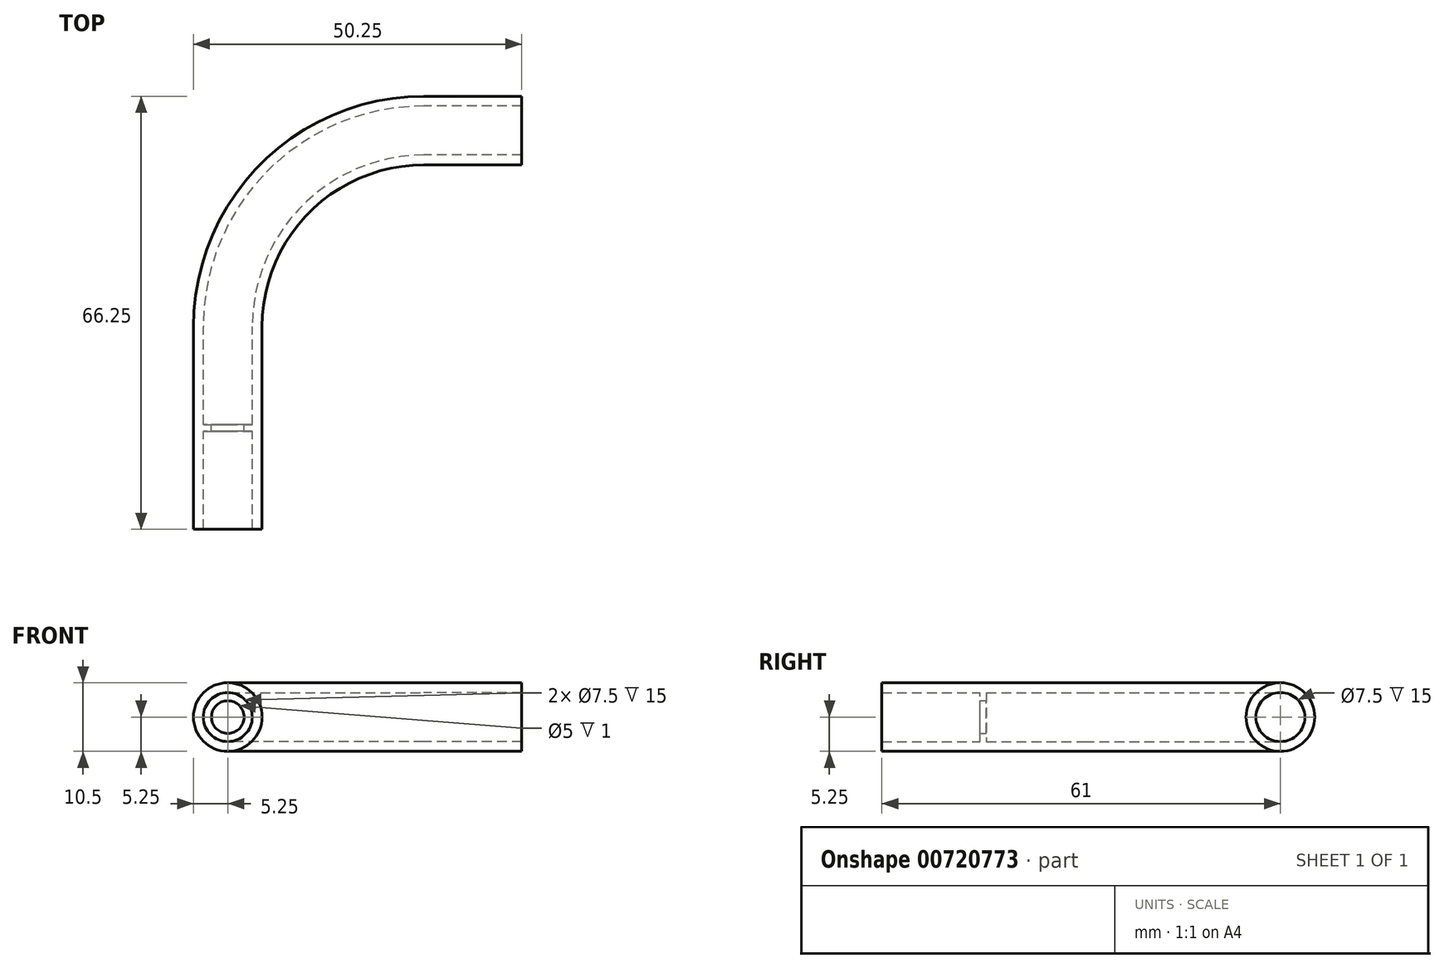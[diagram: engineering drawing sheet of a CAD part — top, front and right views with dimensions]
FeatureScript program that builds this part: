
annotation { "Feature Type Name" : "Feature", "Feature Type Description" : "" }
export const myFeature = defineFeature(function(context is Context, id is Id, definition is map)
    precondition{}
    {
        {
            var Q0;
            Q0=qCreatedBy(makeId("Top.planeOp"),FACE);
            var sketch = newSketch(context, id + "F0", { "sketchPlane" : qUnion([Q0])});
            skCircle(sketch, "E0", {"center": v(0, 0) * mm, "radius": 30 * mm, "construction": true});
            skLineSegment(sketch, "E1", {"start": v(-30, 0) * mm, "end": v(-30, -15) * mm, "construction": true});
            skLineSegment(sketch, "E2", {"start": v(0, 30) * mm, "end": v(15, 30) * mm});
            skLineSegment(sketch, "E3", {"start": v(-35.25, 0) * mm, "end": v(-24.75, 0) * mm});
            skLineSegment(sketch, "E4", {"start": v(-30, 0) * mm, "end": v(-30, 0) * mm});
            skLineSegment(sketch, "E5.top", {"start": v(-35.25, -15) * mm, "end": v(-24.75, -15) * mm});
            skLineSegment(sketch, "E5.left", {"start": v(-35.25, 0) * mm, "end": v(-35.25, -15) * mm});
            skLineSegment(sketch, "E5.right", {"start": v(-24.75, 0) * mm, "end": v(-24.75, -15) * mm});
            skLineSegment(sketch, "E6.bottom", {"start": v(0, 35.25) * mm, "end": v(15, 35.25) * mm});
            skLineSegment(sketch, "E6.top", {"start": v(0, 24.75) * mm, "end": v(15, 24.75) * mm});
            skLineSegment(sketch, "E6.left", {"start": v(0, 35.25) * mm, "end": v(0, 24.75) * mm});
            skLineSegment(sketch, "E6.right", {"start": v(15, 35.25) * mm, "end": v(15, 24.75) * mm});
            skLineSegment(sketch, "E7", {"start": v(0, 30) * mm, "end": v(0, 30) * mm});
            skLineSegment(sketch, "E8.bottom", {"start": v(0, 33.75) * mm, "end": v(15, 33.75) * mm});
            skLineSegment(sketch, "E8.top", {"start": v(0, 26.25) * mm, "end": v(15, 26.25) * mm});
            skLineSegment(sketch, "E8.left", {"start": v(0, 33.75) * mm, "end": v(0, 26.25) * mm});
            skLineSegment(sketch, "E8.right", {"start": v(15, 33.75) * mm, "end": v(15, 26.25) * mm});
            skLineSegment(sketch, "E9.bottom", {"start": v(-33.75, 0) * mm, "end": v(-26.25, 0) * mm});
            skLineSegment(sketch, "E9.top", {"start": v(-33.75, -15) * mm, "end": v(-26.25, -15) * mm});
            skLineSegment(sketch, "E9.left", {"start": v(-33.75, 0) * mm, "end": v(-33.75, -15) * mm});
            skLineSegment(sketch, "E9.right", {"start": v(-26.25, 0) * mm, "end": v(-26.25, -15) * mm});
            skSolve(sketch);
        }
        {
            var Q0;
            {var subQ0=sQuery(id+"F0.wireOp",EDGE,"E5.left");Q0=makeQuery(id+"F0.imprint","IMPRINT",FACE,{"disambiguationData":[TD([[makeQuery(id+"F0.imprint","IMPRINT",EDGE,{"derivedFrom":subQ0}),1.0]])]});}
            var Q1;
            {var subQ0=sQuery(id+"F0.wireOp",EDGE,"E5.right");Q1=makeQuery(id+"F0.imprint","IMPRINT",FACE,{"disambiguationData":[TD([[makeQuery(id+"F0.imprint","IMPRINT",EDGE,{"derivedFrom":subQ0}),-1.0]])]});}
            var Q2;
            Q2=sQuery(id+"F0.wireOp",EDGE,"E1");
            revolve(context, id + "F1", {"surfaceOperationType" : NewSurfaceOperationType.NEW, "entities" : qUnion([Q0, Q1]), "axis" : qUnion([Q2]), "revolveType" : RevolveType.FULL});
        }
        {
            var Q0;
            Q0=qCreatedBy(makeId("Top.planeOp"),FACE);
            var sketch = newSketch(context, id + "F2", { "sketchPlane" : qUnion([Q0])});
            skLineSegment(sketch, "E10", {"start": v(0, 0) * mm, "end": v(0, 30) * mm, "construction": true});
            skLineSegment(sketch, "E11", {"start": v(0, 30) * mm, "end": v(32.05, 30) * mm, "construction": true});
            skSolve(sketch);
        }
        {
            var Q0;
            {var subQ0=sQuery(id+"F0.wireOp",EDGE,"E6.top");Q0=makeQuery(id+"F0.imprint","IMPRINT",FACE,{"disambiguationData":[TD([[makeQuery(id+"F0.imprint","IMPRINT",EDGE,{"derivedFrom":subQ0}),1.0]])]});}
            var Q1;
            {var subQ0=sQuery(id+"F0.wireOp",EDGE,"E6.bottom");Q1=makeQuery(id+"F0.imprint","IMPRINT",FACE,{"disambiguationData":[TD([[makeQuery(id+"F0.imprint","IMPRINT",EDGE,{"derivedFrom":subQ0}),-1.0]])]});}
            var Q2;
            Q2=sQuery(id+"F2.wireOp",EDGE,"E11");
            revolve(context, id + "F3", {"operationType" : NewBodyOperationType.ADD, "surfaceOperationType" : NewSurfaceOperationType.NEW, "entities" : qUnion([Q0, Q1]), "axis" : qUnion([Q2]), "revolveType" : RevolveType.FULL});
        }
        {
            var Q0;
            Q0=qCreatedBy(makeId("Top.planeOp"),FACE);
            var sketch = newSketch(context, id + "F4", { "sketchPlane" : qUnion([Q0])});
            skLineSegment(sketch, "E12", {"start": v(0, 0) * mm, "end": v(-30, 0) * mm, "construction": true});
            skLineSegment(sketch, "E13", {"start": v(0, 0) * mm, "end": v(0, 30) * mm, "construction": true});
            skArc(sketch, "E14", {"start": v(-30, 0) * mm, "mid": v(-21.21, 21.21) * mm, "end": v(0, 30) * mm});
            skSolve(sketch);
        }
        {
            var Q0;
            {var subQ0=sQuery(id+"F0.wireOp",EDGE,"E3");Q0=makeQuery(id+"F1.opRevolve","SWEPT_FACE",FACE,{"disambiguationData":[OSD([subQ0]),TDD([makeQuery(id+"F0.imprint","IMPRINT",EDGE,{"disambiguationData":[TD([[makeQuery(id+"F0.imprint","INTERSECT",VERTEX,{"derivedFrom":[subQ0,sQuery(id+"F0.wireOp",EDGE,"E5.left")]}),-1.0]])],"derivedFrom":subQ0})])]});}
            var Q1;
            {var subQ0=sQuery(id+"F0.wireOp",EDGE,"E6.left");Q1=makeQuery(id+"F3.opRevolve","SWEPT_FACE",FACE,{"disambiguationData":[OSD([subQ0]),TDD([makeQuery(id+"F0.imprint","IMPRINT",EDGE,{"disambiguationData":[TD([[makeQuery(id+"F0.imprint","INTERSECT",VERTEX,{"derivedFrom":[sQuery(id+"F0.wireOp",EDGE,"E6.bottom"),subQ0]}),-1.0]])],"derivedFrom":subQ0})])]});}
            var Q2;
            Q2=sQuery(id+"F4.wireOp",EDGE,"E14");
            sweep(context, id + "F5", {"operationType" : NewBodyOperationType.ADD, "profiles" : qUnion([Q0, Q1]), "path" : qUnion([Q2])});
        }
        {
            var Q0;
            {var subQ0=sQuery(id+"F0.wireOp",EDGE,"E5.top");Q0=makeQuery(id+"F1.opRevolve","SWEPT_FACE",FACE,{"disambiguationData":[OSD([subQ0]),TDD([makeQuery(id+"F0.imprint","IMPRINT",EDGE,{"disambiguationData":[TD([[makeQuery(id+"F0.imprint","INTERSECT",VERTEX,{"derivedFrom":[subQ0,sQuery(id+"F0.wireOp",EDGE,"E5.left")]}),-1.0]])],"derivedFrom":subQ0})])]});}
            var sketch = newSketch(context, id + "F6", { "sketchPlane" : qUnion([Q0])});
            skCircle(sketch, "E15", {"center": v(-30, 0) * mm, "radius": 5.25 * mm});
            skCircle(sketch, "E16", {"center": v(-30, 0) * mm, "radius": 2.5 * mm});
            skSolve(sketch);
        }
        {
            var Q0;
            Q0=makeQuery(id+"F6.imprint","IMPRINT",FACE,{"disambiguationData":[TD([[makeQuery(id+"F6.imprint","IMPRINT",EDGE,{"derivedFrom":sQuery(id+"F6.wireOp",EDGE,"E15")}),-1.0]])]});
            var Q1;
            Q1=makeQuery(id+"F6.imprint","IMPRINT",FACE,{"disambiguationData":[TD([[makeQuery(id+"F6.imprint","IMPRINT",EDGE,{"derivedFrom":sQuery(id+"F6.wireOp",EDGE,"E16")}),-1.0]])]});
            extrude(context, id + "F7", {"entities" : qUnion([Q0, Q1]), "operationType" : NewBodyOperationType.ADD, "depth" : 1 * mm, "offsetDistance" : 25 * mm});
        }
        {
            var Q0;
            Q0=makeQuery(id+"F7.opExtrude","CAP_FACE",FACE,{"disambiguationData":[OSD([sQuery(id+"F6.wireOp",EDGE,"E15"),sQuery(id+"F6.wireOp",EDGE,"E16")])],"isStart":false});
            var sketch = newSketch(context, id + "F8", { "sketchPlane" : qUnion([Q0])});
            skCircle(sketch, "E17", {"center": v(-30, 0) * mm, "radius": 5.25 * mm});
            skCircle(sketch, "E18", {"center": v(-30, 0) * mm, "radius": 3.75 * mm});
            skSolve(sketch);
        }
        {
            var Q0;
            Q0=makeQuery(id+"F8.imprint","IMPRINT",FACE,{"disambiguationData":[TD([[makeQuery(id+"F8.imprint","IMPRINT",EDGE,{"derivedFrom":sQuery(id+"F8.wireOp",EDGE,"E17")}),-1.0]])]});
            extrude(context, id + "F9", {"entities" : qUnion([Q0]), "operationType" : NewBodyOperationType.ADD, "depth" : 15 * mm, "offsetDistance" : 25 * mm});
        }
    });
